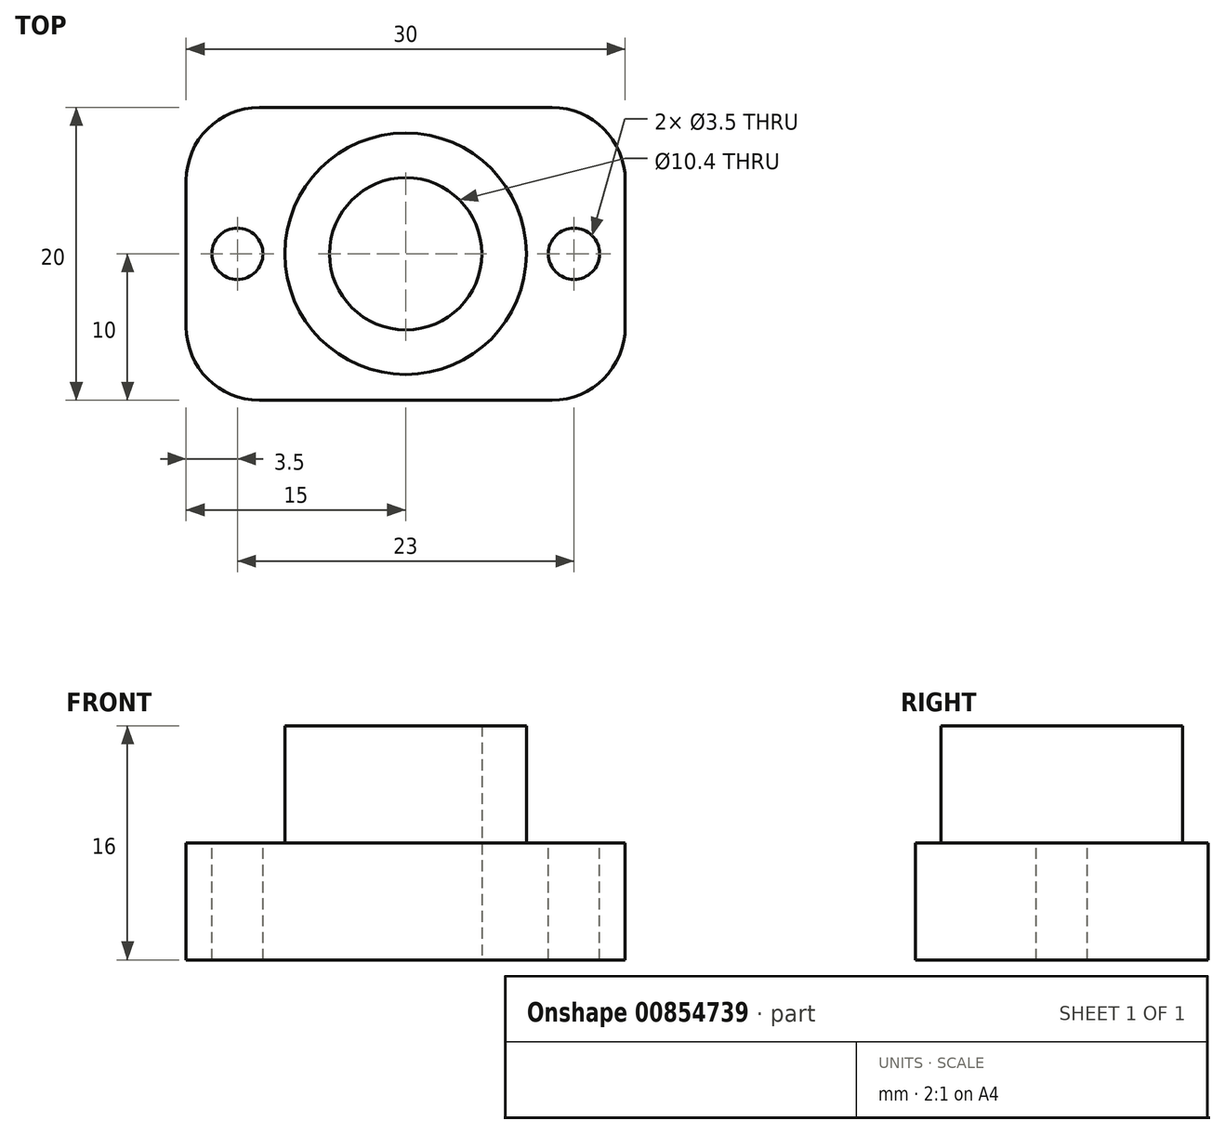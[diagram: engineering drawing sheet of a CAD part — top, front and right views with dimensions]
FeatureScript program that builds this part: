
annotation { "Feature Type Name" : "Feature", "Feature Type Description" : "" }
export const myFeature = defineFeature(function(context is Context, id is Id, definition is map)
    precondition{}
    {
        {
            var Q0;
            Q0=qCreatedBy(makeId("Top.planeOp"),FACE);
            var sketch = newSketch(context, id + "F0", { "sketchPlane" : qUnion([Q0])});
            skLineSegment(sketch, "E0.bottom", {"start": v(0, 0) * mm, "end": v(30, 0) * mm});
            skLineSegment(sketch, "E0.top", {"start": v(0, 20) * mm, "end": v(30, 20) * mm});
            skLineSegment(sketch, "E0.left", {"start": v(0, 0) * mm, "end": v(0, 20) * mm});
            skLineSegment(sketch, "E0.right", {"start": v(30, 0) * mm, "end": v(30, 20) * mm});
            skSolve(sketch);
        }
        {
            var Q0;
            Q0 = qSketchRegion(id + "F0", true);
            extrude(context, id + "F1", {"entities" : qUnion([Q0]), "depth" : 8 * mm, "offsetDistance" : 25 * mm});
        }
        {
            var Q0;
            Q0=makeQuery(id+"F1.opExtrude","CAP_FACE",FACE,{"disambiguationData":[OSD([sQuery(id+"F0.wireOp",EDGE,"E0.bottom"),sQuery(id+"F0.wireOp",EDGE,"E0.top"),sQuery(id+"F0.wireOp",EDGE,"E0.left"),sQuery(id+"F0.wireOp",EDGE,"E0.right")])],"isStart":false});
            var sketch = newSketch(context, id + "F2", { "sketchPlane" : qUnion([Q0])});
            skCircle(sketch, "E1", {"center": v(15, 10) * mm, "radius": 5.2 * mm});
            skPoint(sketch, "E1.centerSnap0", {"position": v(15, 0) * mm});
            skPoint(sketch, "E1.centerSnap1", {"position": v(0, 10) * mm});
            skCircle(sketch, "E2", {"center": v(15, 10) * mm, "radius": 8.25 * mm});
            skSolve(sketch);
        }
        {
            var Q0;
            Q0 = qSketchRegion(id + "F2", true);
            extrude(context, id + "F3", {"entities" : qUnion([Q0]), "operationType" : NewBodyOperationType.ADD, "depth" : 8 * mm, "offsetDistance" : 25 * mm});
        }
        {
            var Q0;
            {var subQ0=sQuery(id+"F0.wireOp",EDGE,"E0.left");var subQ1=sQuery(id+"F0.wireOp",EDGE,"E0.top");var subQ2=sQuery(id+"F0.wireOp",EDGE,"E0.right");var subQ3=sQuery(id+"F0.wireOp",EDGE,"E0.bottom");Q0=makeQuery(id+"F3.boolean.opBoolean","SPLIT",FACE,{"disambiguationData":[TD([makeQuery(id+"F1.opExtrude","SWEPT_FACE",FACE,{"disambiguationData":[OSD([subQ3])]})])],"derivedFrom":makeQuery(id+"F1.opExtrude","CAP_FACE",FACE,{"disambiguationData":[OSD([subQ3,subQ1,subQ0,subQ2])],"isStart":false})});}
            var sketch = newSketch(context, id + "F4", { "sketchPlane" : qUnion([Q0])});
            skCircle(sketch, "E3", {"center": v(3.5, 10) * mm, "radius": 1.75 * mm});
            skPoint(sketch, "E3.centerSnap0", {"position": v(0, 10) * mm});
            skCircle(sketch, "E4", {"center": v(26.5, 10) * mm, "radius": 1.75 * mm});
            skPoint(sketch, "E4.centerSnap0", {"position": v(30, 10) * mm});
            skCircle(sketch, "E5", {"center": v(15, 10) * mm, "radius": 5.2 * mm});
            skSolve(sketch);
        }
        {
            var Q0;
            Q0 = qSketchRegion(id + "F4", true);
            extrude(context, id + "F5", {"entities" : qUnion([Q0]), "operationType" : NewBodyOperationType.REMOVE, "oppositeDirection" : true, "depth" : 25 * mm, "offsetDistance" : 25 * mm});
        }
        {
            var Q0;
            Q0=makeQuery(id+"F1.opExtrude","SWEPT_EDGE",EDGE,{"disambiguationData":[OSD([sQuery(id+"F0.wireOp",EDGE,"E0.bottom"),sQuery(id+"F0.wireOp",EDGE,"E0.left")])]});
            var Q1;
            Q1=makeQuery(id+"F1.opExtrude","SWEPT_EDGE",EDGE,{"disambiguationData":[OSD([sQuery(id+"F0.wireOp",EDGE,"E0.bottom"),sQuery(id+"F0.wireOp",EDGE,"E0.right")])]});
            var Q2;
            Q2=makeQuery(id+"F1.opExtrude","SWEPT_EDGE",EDGE,{"disambiguationData":[OSD([sQuery(id+"F0.wireOp",EDGE,"E0.top"),sQuery(id+"F0.wireOp",EDGE,"E0.right")])]});
            var Q3;
            Q3=makeQuery(id+"F1.opExtrude","SWEPT_EDGE",EDGE,{"disambiguationData":[OSD([sQuery(id+"F0.wireOp",EDGE,"E0.top"),sQuery(id+"F0.wireOp",EDGE,"E0.left")])]});
            fillet(context, id + "F6", {"entities" : qUnion([Q0, Q1, Q2, Q3]), "radius" : 5 * mm, "tangentPropagation" : true, "allowEdgeOverflow" : false});
        }
    });
